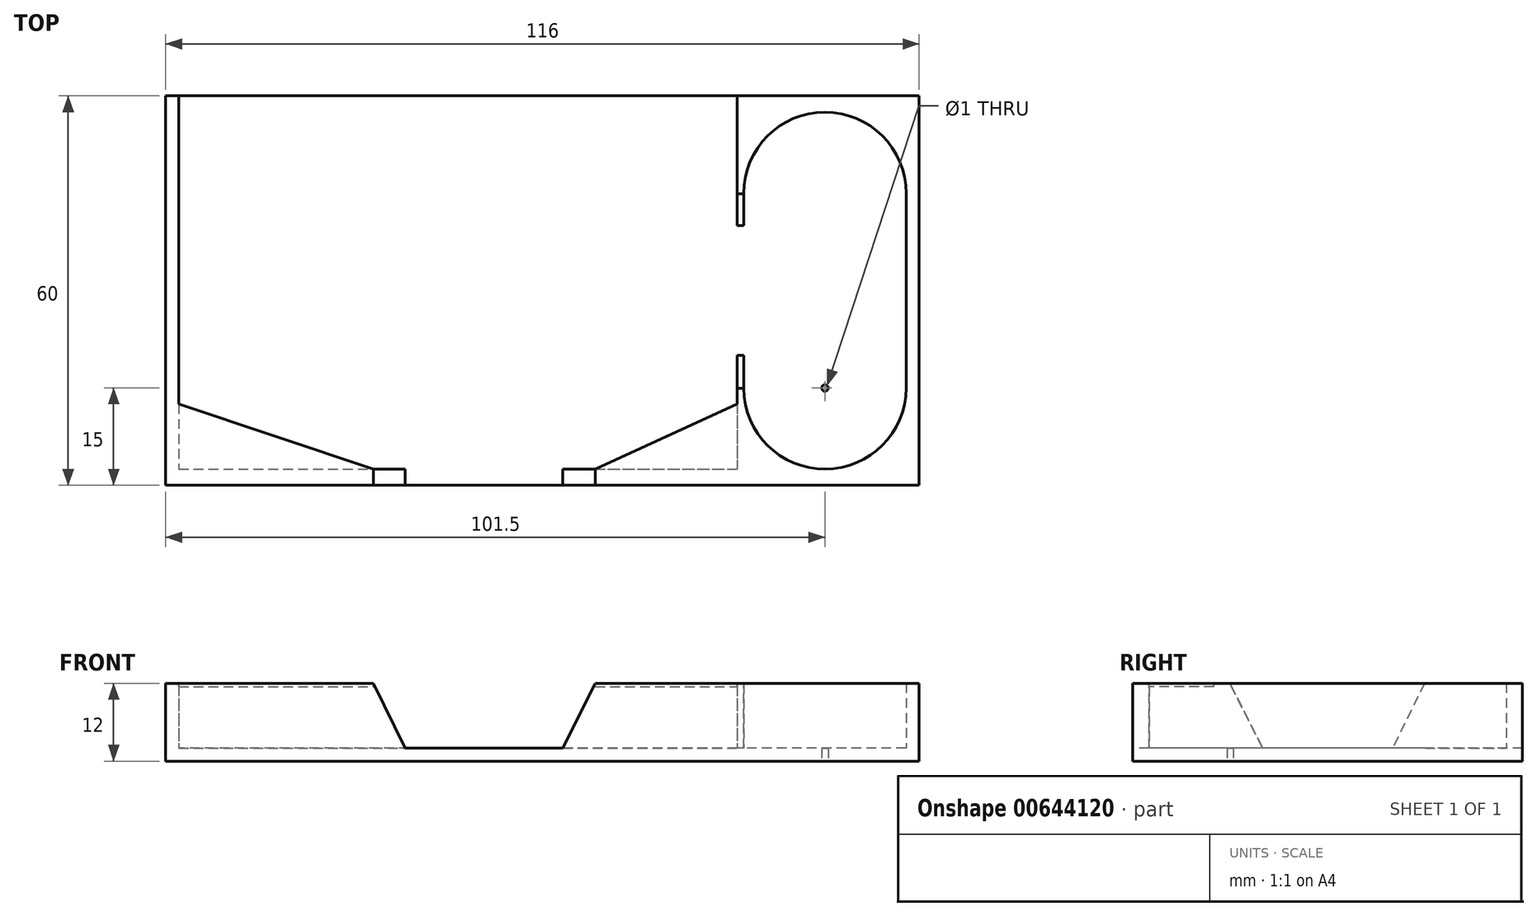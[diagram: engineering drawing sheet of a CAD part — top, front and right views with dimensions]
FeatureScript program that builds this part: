
annotation { "Feature Type Name" : "Feature", "Feature Type Description" : "" }
export const myFeature = defineFeature(function(context is Context, id is Id, definition is map)
    precondition{}
    {
        {
            var Q0;
            Q0=qCreatedBy(makeId("Top.planeOp"),FACE);
            var sketch = newSketch(context, id + "F0", { "sketchPlane" : qUnion([Q0])});
            skLineSegment(sketch, "E0.bottom", {"start": v(58, -30) * mm, "end": v(-58, -30) * mm});
            skLineSegment(sketch, "E0.top", {"start": v(58, 30) * mm, "end": v(-58, 30) * mm});
            skLineSegment(sketch, "E0.left", {"start": v(58, -30) * mm, "end": v(58, 30) * mm});
            skLineSegment(sketch, "E0.right", {"start": v(-58, -30) * mm, "end": v(-58, 30) * mm});
            skPoint(sketch, "E0.middle", {"position": v(0, 0) * mm});
            skLineSegment(sketch, "E1.left", {"start": v(56, 15) * mm, "end": v(56, -15) * mm});
            skLineSegment(sketch, "E1.right", {"start": v(31, 15) * mm, "end": v(31, -15) * mm});
            skLineSegment(sketch, "E2.bottom", {"start": v(-56, 30) * mm, "end": v(30, 30) * mm});
            skLineSegment(sketch, "E2.top", {"start": v(-56, -27.5) * mm, "end": v(30, -27.5) * mm});
            skLineSegment(sketch, "E2.left", {"start": v(-56, 30) * mm, "end": v(-56, -27.5) * mm});
            skLineSegment(sketch, "E2.right", {"start": v(30, 30) * mm, "end": v(30, -27.5) * mm});
            skLineSegment(sketch, "E3", {"start": v(31, 15) * mm, "end": v(56, 15) * mm, "construction": true});
            skArc(sketch, "E4", {"start": v(56, 15) * mm, "mid": v(43.5, 27.5) * mm, "end": v(31, 15) * mm});
            skPoint(sketch, "E4.third.point", {"position": v(43.5, 27.5) * mm});
            skPoint(sketch, "E5.orphan", {"position": v(31, 27.5) * mm});
            skPoint(sketch, "E6.orphan", {"position": v(56, 27.5) * mm});
            skLineSegment(sketch, "E7", {"start": v(31, -15) * mm, "end": v(56, -15) * mm, "construction": true});
            skArc(sketch, "E8", {"start": v(31, -15) * mm, "mid": v(43.5, -27.5) * mm, "end": v(56, -15) * mm});
            skSolve(sketch);
        }
        {
            var Q0;
            Q0=makeQuery(id+"F0.imprint","IMPRINT",FACE,{"disambiguationData":[TD([[makeQuery(id+"F0.imprint","IMPRINT",EDGE,{"derivedFrom":sQuery(id+"F0.wireOp",EDGE,"E0.bottom")}),-1.0]])]});
            extrude(context, id + "F1", {"entities" : qUnion([Q0]), "depth" : 10 * mm, "offsetDistance" : 25 * mm});
        }
        {
            var Q0;
            Q0=makeQuery(id+"F1.opExtrude","CAP_FACE",FACE,{"disambiguationData":[OSD([sQuery(id+"F0.wireOp",EDGE,"E0.bottom"),sQuery(id+"F0.wireOp",EDGE,"E0.top"),sQuery(id+"F0.wireOp",EDGE,"E0.left"),sQuery(id+"F0.wireOp",EDGE,"E0.right"),sQuery(id+"F0.wireOp",EDGE,"E1.left"),sQuery(id+"F0.wireOp",EDGE,"E1.right"),sQuery(id+"F0.wireOp",EDGE,"E2.top"),sQuery(id+"F0.wireOp",EDGE,"E2.left"),sQuery(id+"F0.wireOp",EDGE,"E2.right"),sQuery(id+"F0.wireOp",EDGE,"E4"),sQuery(id+"F0.wireOp",EDGE,"E8")])],"isStart":true});
            var sketch = newSketch(context, id + "F2", { "sketchPlane" : qUnion([Q0])});
            skLineSegment(sketch, "E9.bottom", {"start": v(58, -30) * mm, "end": v(-58, -30) * mm});
            skLineSegment(sketch, "E9.top", {"start": v(58, 30) * mm, "end": v(-58, 30) * mm});
            skLineSegment(sketch, "E9.left", {"start": v(58, -30) * mm, "end": v(58, 30) * mm});
            skLineSegment(sketch, "E9.right", {"start": v(-58, -30) * mm, "end": v(-58, 30) * mm});
            skSolve(sketch);
        }
        {
            var Q0;
            Q0=makeQuery(id+"F2.imprint","IMPRINT",FACE,{"disambiguationData":[TD([[makeQuery(id+"F2.imprint","IMPRINT",EDGE,{"derivedFrom":makeQuery(id+"F1.opExtrude","CAP_EDGE",EDGE,{"disambiguationData":[OSD([sQuery(id+"F0.wireOp",EDGE,"E1.left")])],"isStart":true})}),1.0]])]});
            var Q1;
            Q1=makeQuery(id+"F2.imprint","IMPRINT",FACE,{"disambiguationData":[TD([[makeQuery(id+"F2.imprint","IMPRINT",EDGE,{"derivedFrom":makeQuery(id+"F1.opExtrude","CAP_EDGE",EDGE,{"disambiguationData":[OSD([sQuery(id+"F0.wireOp",EDGE,"E2.top")])],"isStart":true})}),-1.0]])]});
            var Q2;
            Q2=makeQuery(id+"F2.imprint","IMPRINT",FACE,{"disambiguationData":[TD([[makeQuery(id+"F2.imprint","IMPRINT",EDGE,{"derivedFrom":sQuery(id+"F2.wireOp",EDGE,"E9.top")}),1.0]])]});
            extrude(context, id + "F3", {"entities" : qUnion([Q0, Q1, Q2]), "operationType" : NewBodyOperationType.ADD, "depth" : 2 * mm, "offsetDistance" : 25 * mm});
        }
        {
            var Q0;
            Q0=makeQuery(id+"F3.boolean.opBoolean","MERGE",FACE,{"derivedFrom":[makeQuery(id+"F1.opExtrude","SWEPT_FACE",FACE,{"disambiguationData":[OSD([sQuery(id+"F0.wireOp",EDGE,"E0.bottom")])]}),makeQuery(id+"F3.opExtrude","SWEPT_FACE",FACE,{"disambiguationData":[OSD([sQuery(id+"F2.wireOp",EDGE,"E9.top")])]})]});
            var sketch = newSketch(context, id + "F4", { "sketchPlane" : qUnion([Q0])});
            skLineSegment(sketch, "E10", {"start": v(38.14, 0) * mm, "end": v(38.14, 10) * mm, "construction": true});
            skLineSegment(sketch, "E11", {"start": v(-58, 10) * mm, "end": v(-26, 10) * mm, "construction": true});
            skLineSegment(sketch, "E12", {"start": v(38.14, 10) * mm, "end": v(8.14, 10) * mm, "construction": true});
            skLineSegment(sketch, "E13", {"start": v(38.14, 0) * mm, "end": v(3.14, 0) * mm, "construction": true});
            skLineSegment(sketch, "E14", {"start": v(-56.16, 0) * mm, "end": v(-21.16, 0) * mm, "construction": true});
            skLineSegment(sketch, "E15", {"start": v(-26, 10) * mm, "end": v(-21.16, 0) * mm});
            skLineSegment(sketch, "E16", {"start": v(3.14, 0) * mm, "end": v(8.14, 10) * mm});
            skLineSegment(sketch, "E17", {"start": v(-26, 10) * mm, "end": v(8.14, 10) * mm});
            skLineSegment(sketch, "E18", {"start": v(3.14, 0) * mm, "end": v(-21.16, 0) * mm});
            skSolve(sketch);
        }
        {
            var Q0;
            Q0=makeQuery(id+"F4.imprint","IMPRINT",FACE,{"disambiguationData":[TD([[makeQuery(id+"F4.imprint","IMPRINT",EDGE,{"derivedFrom":sQuery(id+"F4.wireOp",EDGE,"E15")}),1.0]])]});
            extrude(context, id + "F5", {"entities" : qUnion([Q0]), "operationType" : NewBodyOperationType.REMOVE, "endBound" : BoundingType.THROUGH_ALL, "oppositeDirection" : true, "depth" : 25 * mm, "offsetDistance" : 25 * mm});
        }
        {
            var Q0;
            {var subQ0=sQuery(id+"F0.wireOp",EDGE,"E0.right");var subQ1=sQuery(id+"F0.wireOp",EDGE,"E0.top");var subQ2=sQuery(id+"F0.wireOp",EDGE,"E2.left");var subQ4=sQuery(id+"F0.wireOp",EDGE,"E0.left");var subQ5=sQuery(id+"F0.wireOp",EDGE,"E2.right");var subQ6=sQuery(id+"F0.wireOp",EDGE,"E0.bottom");var subQ7=sQuery(id+"F0.wireOp",EDGE,"E2.top");Q0=makeQuery(id+"F5.boolean.opBoolean","SPLIT",FACE,{"disambiguationData":[TD([makeQuery(id+"F1.opExtrude","SWEPT_FACE",FACE,{"disambiguationData":[OSD([subQ0])]})])],"derivedFrom":makeQuery(id+"F1.opExtrude","CAP_FACE",FACE,{"disambiguationData":[OSD([subQ6,subQ1,subQ4,subQ0,sQuery(id+"F0.wireOp",EDGE,"E1.left"),sQuery(id+"F0.wireOp",EDGE,"E1.right"),subQ7,subQ2,subQ5,sQuery(id+"F0.wireOp",EDGE,"E4"),sQuery(id+"F0.wireOp",EDGE,"E8")])],"isStart":false})});}
            var sketch = newSketch(context, id + "F6", { "sketchPlane" : qUnion([Q0])});
            skLineSegment(sketch, "E19", {"start": v(-26, -27.5) * mm, "end": v(-56, -17.5) * mm});
            skSolve(sketch);
        }
        {
            var Q0;
            {var subQ0=sQuery(id+"F6.wireOp",EDGE,"E19");Q0=makeQuery(id+"F6.imprint","IMPRINT",FACE,{"disambiguationData":[TD([[makeQuery(id+"F6.imprint","IMPRINT",EDGE,{"derivedFrom":subQ0}),1.0]])]});}
            extrude(context, id + "F7", {"entities" : qUnion([Q0]), "operationType" : NewBodyOperationType.ADD, "depth" : -0.5 * mm, "offsetDistance" : 25 * mm});
        }
        {
            var Q0;
            {var subQ0=sQuery(id+"F0.wireOp",EDGE,"E8");var subQ1=sQuery(id+"F0.wireOp",EDGE,"E4");var subQ2=sQuery(id+"F0.wireOp",EDGE,"E2.top");var subQ3=sQuery(id+"F0.wireOp",EDGE,"E1.right");var subQ4=sQuery(id+"F0.wireOp",EDGE,"E1.left");var subQ5=sQuery(id+"F0.wireOp",EDGE,"E2.right");var subQ6=sQuery(id+"F0.wireOp",EDGE,"E0.bottom");var subQ7=sQuery(id+"F0.wireOp",EDGE,"E0.left");var subQ8=sQuery(id+"F0.wireOp",EDGE,"E0.top");var subQ10=sQuery(id+"F0.wireOp",EDGE,"E0.right");var subQ11=sQuery(id+"F0.wireOp",EDGE,"E2.left");Q0=makeQuery(id+"F5.boolean.opBoolean","SPLIT",FACE,{"disambiguationData":[TD([makeQuery(id+"F1.opExtrude","SWEPT_FACE",FACE,{"disambiguationData":[OSD([subQ7])]})])],"derivedFrom":makeQuery(id+"F1.opExtrude","CAP_FACE",FACE,{"disambiguationData":[OSD([subQ6,subQ8,subQ7,subQ10,subQ4,subQ3,subQ2,subQ11,subQ5,subQ1,subQ0])],"isStart":false})});}
            var sketch = newSketch(context, id + "F8", { "sketchPlane" : qUnion([Q0])});
            skLineSegment(sketch, "E20", {"start": v(8.14, -27.5) * mm, "end": v(30, -17.5) * mm});
            skSolve(sketch);
        }
        {
            var Q0;
            {var subQ0=sQuery(id+"F8.wireOp",EDGE,"E20");Q0=makeQuery(id+"F8.imprint","IMPRINT",FACE,{"disambiguationData":[TD([[makeQuery(id+"F8.imprint","IMPRINT",EDGE,{"derivedFrom":subQ0}),-1.0]])]});}
            extrude(context, id + "F9", {"entities" : qUnion([Q0]), "operationType" : NewBodyOperationType.ADD, "depth" : -0.5 * mm, "offsetDistance" : 25 * mm});
        }
        {
            var Q0;
            Q0=makeQuery(id+"F3.opExtrude","CAP_FACE",FACE,{"disambiguationData":[OSD([sQuery(id+"F2.wireOp",EDGE,"E9.bottom"),sQuery(id+"F2.wireOp",EDGE,"E9.top"),sQuery(id+"F2.wireOp",EDGE,"E9.left"),sQuery(id+"F2.wireOp",EDGE,"E9.right")])],"isStart":false});
            var sketch = newSketch(context, id + "F10", { "sketchPlane" : qUnion([Q0])});
            skCircle(sketch, "E21", {"center": v(43.5, 15) * mm, "radius": 0.5 * mm});
            skSolve(sketch);
        }
        {
            var Q0;
            Q0=makeQuery(id+"F10.imprint","IMPRINT",FACE,{"disambiguationData":[TD([[makeQuery(id+"F10.imprint","IMPRINT",EDGE,{"derivedFrom":sQuery(id+"F10.wireOp",EDGE,"E21")}),1.0]])]});
            extrude(context, id + "F11", {"entities" : qUnion([Q0]), "operationType" : NewBodyOperationType.REMOVE, "endBound" : BoundingType.THROUGH_ALL, "oppositeDirection" : true, "depth" : 25 * mm, "offsetDistance" : 25 * mm});
        }
        {
            var Q0;
            Q0=makeQuery(id+"F1.opExtrude","SWEPT_FACE",FACE,{"disambiguationData":[OSD([sQuery(id+"F0.wireOp",EDGE,"E2.right")])]});
            var sketch = newSketch(context, id + "F12", { "sketchPlane" : qUnion([Q0])});
            skLineSegment(sketch, "E22", {"start": v(-14.93, 10) * mm, "end": v(-10, 0) * mm});
            skLineSegment(sketch, "E23", {"start": v(-10, 0) * mm, "end": v(10, 0) * mm});
            skLineSegment(sketch, "E24", {"start": v(10, 0) * mm, "end": v(15.07, 10) * mm});
            skLineSegment(sketch, "E25", {"start": v(15.07, 10) * mm, "end": v(-14.93, 10) * mm});
            skSolve(sketch);
        }
        {
            var Q0;
            Q0=makeQuery(id+"F12.imprint","IMPRINT",FACE,{"disambiguationData":[TD([[makeQuery(id+"F12.imprint","IMPRINT",EDGE,{"derivedFrom":sQuery(id+"F12.wireOp",EDGE,"E22")}),1.0]])]});
            extrude(context, id + "F13", {"entities" : qUnion([Q0]), "operationType" : NewBodyOperationType.REMOVE, "oppositeDirection" : true, "depth" : 3 * mm, "offsetDistance" : 25 * mm});
        }
    });
